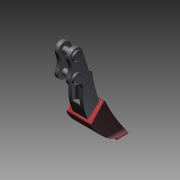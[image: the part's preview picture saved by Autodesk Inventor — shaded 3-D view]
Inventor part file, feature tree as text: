
AUTODESK INVENTOR PART (.ipt)
format: ipt  version: 2011 SP1 (Build 150282100, 282)  size: 242,176 bytes
history: native  units: mm
features: other x21, sketch x6, extrude x4, revolve x2
ambient origin geometry x8: Origin, YZ Plane, XZ Plane, XY Plane, X Axis, Y Axis, Z Axis, Center Point
bodies: Solid1 (feature_tree)
feature tree (33):
  extrude  "Extrusion1"  Depth=100.0mm TaperAngle=0.0deg
  extrude  "Extrusion2"  Depth=20.0mm TaperAngle=0.0deg
  extrude  "Extrusion3"  TaperAngle=360.0deg  [1 undecoded]
  extrude  "Extrusion4"  [1 undecoded]
  sketch  "Skizze_5"
  sketch  "Skizze_6"
  revolve  "Revolution1"  [1 undecoded]
  revolve  "Revolution2"  [1 undecoded]
  other  "HG1_XY"
  other  "HG1_YZ"
  other  "HG1_ZX"
  other  "HG1_X"
  other  "HG1_Y"
  other  "HG1_Z"
  other  "HG1_Center"
  other  "HG2_XY"
  other  "HG2_YZ"
  other  "HG2_ZX"
  other  "HG2_X"
  other  "HG2_Y"
  other  "HG2_Z"
  other  "HG2_Center"
  other  "end_XY"
  other  "end_YZ"
  other  "end_ZX"
  other  "end_X"
  other  "end_Y"
  other  "end_Z"
  other  "end_Center"
  sketch  "Skizze_1"  dims[d0=20.0mm d1=0.0mm d2=100.0mm d3=0.0mm]
  sketch  "Skizze_2"  dims[d4=24.0mm d5=0.0mm d6=20.0mm d7=0.0mm]
  sketch  "Skizze_3"  dims[d8=360.0deg d9=360.0deg]
  sketch  "Skizze_4"
note: 4 required parameter values undecoded (feature->parameter linkage not recoverable at this tier; creation-order binding heuristic only, values carry confidence <= 0.55)
